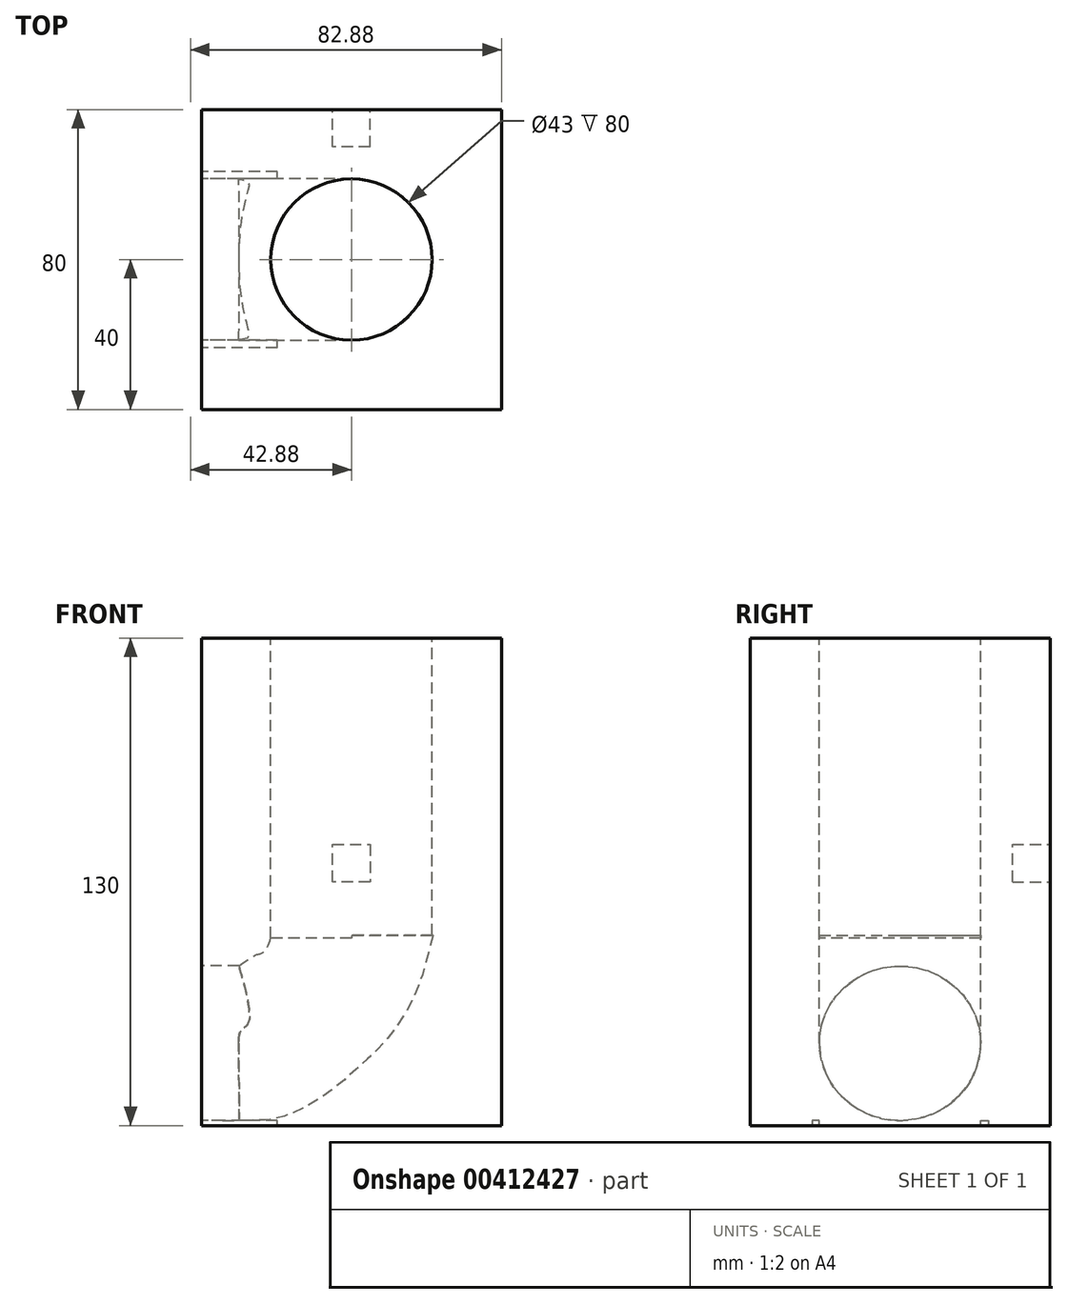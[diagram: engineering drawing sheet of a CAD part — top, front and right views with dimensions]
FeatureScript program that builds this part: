
annotation { "Feature Type Name" : "Feature", "Feature Type Description" : "" }
export const myFeature = defineFeature(function(context is Context, id is Id, definition is map)
    precondition{}
    {
        {
            var Q0;
            Q0=qCreatedBy(makeId("Top.planeOp"),FACE);
            var sketch = newSketch(context, id + "F0", { "sketchPlane" : qUnion([Q0])});
            skLineSegment(sketch, "E0.bottom", {"start": v(40, -40) * mm, "end": v(-40, -40) * mm});
            skLineSegment(sketch, "E0.top", {"start": v(40, 40) * mm, "end": v(-40, 40) * mm});
            skLineSegment(sketch, "E0.left", {"start": v(40, -40) * mm, "end": v(40, 40) * mm});
            skLineSegment(sketch, "E0.right", {"start": v(-40, -40) * mm, "end": v(-40, 40) * mm});
            skPoint(sketch, "E0.middle", {"position": v(0, 0) * mm});
            skSolve(sketch);
        }
        {
            var Q0;
            Q0=makeQuery(id+"F0.imprint","IMPRINT",FACE,{"disambiguationData":[TD([[makeQuery(id+"F0.imprint","IMPRINT",EDGE,{"derivedFrom":sQuery(id+"F0.wireOp",EDGE,"E0.bottom")}),-1.0]])]});
            extrude(context, id + "F1", {"entities" : qUnion([Q0]), "depth" : 130 * mm});
        }
        {
            var Q0;
            Q0=makeQuery(id+"F1.opExtrude","CAP_FACE",FACE,{"disambiguationData":[OSD([sQuery(id+"F0.wireOp",EDGE,"E0.bottom"),sQuery(id+"F0.wireOp",EDGE,"E0.top"),sQuery(id+"F0.wireOp",EDGE,"E0.left"),sQuery(id+"F0.wireOp",EDGE,"E0.right")])],"isStart":false});
            var sketch = newSketch(context, id + "F2", { "sketchPlane" : qUnion([Q0])});
            skCircle(sketch, "E1", {"center": v(0, 0) * mm, "radius": 21.5 * mm});
            skSolve(sketch);
        }
        {
            var Q0;
            Q0=makeQuery(id+"F2.imprint","IMPRINT",FACE,{"disambiguationData":[TD([[makeQuery(id+"F2.imprint","IMPRINT",EDGE,{"derivedFrom":sQuery(id+"F2.wireOp",EDGE,"E1")}),1.0]])]});
            extrude(context, id + "F3", {"entities" : qUnion([Q0]), "operationType" : NewBodyOperationType.REMOVE, "oppositeDirection" : true, "depth" : 80 * mm});
        }
        {
            var Q0;
            Q0=makeQuery(id+"F1.opExtrude","SWEPT_FACE",FACE,{"disambiguationData":[OSD([sQuery(id+"F0.wireOp",EDGE,"E0.top")])]});
            cPlane(context, id + "F4", {"entities" : qUnion([Q0]), "cplaneType" : CPlaneType.OFFSET, "offset" : 40 * mm, "oppositeDirection" : true, "width" : 150 * mm, "height" : 150 * mm});
        }
        {
            var Q0;
            Q0=qCreatedBy(id+"F4.planeOp",FACE);
            var sketch = newSketch(context, id + "F5", { "sketchPlane" : qUnion([Q0])});
            skPoint(sketch, "E2.0.internal.orphan", {"position": v(0, 50.77) * mm});
            skLineSegment(sketch, "E3", {"start": v(40.5, 22.17) * mm, "end": v(30.1, 22.17) * mm});
            skFitSpline(sketch, "E4", {"points": [v(0, 50.77) * mm, v(4.24, 40.15) * mm, v(14.18, 29.43) * mm, v(24.13, 23) * mm, v(30.1, 22.17) * mm], "startDerivative": vector(12.32, -41.84) * mm, "endDerivative": vector(30.55, -0.59) * mm});
            skLineSegment(sketch, "E5", {"start": v(40.5, 22.17) * mm, "end": v(52.8, 22.17) * mm});
            skSolve(sketch);
        }
        {
            var Q0;
            Q0=makeQuery(id+"F3.boolean.opBoolean","COPY",FACE,{"derivedFrom":makeQuery(id+"F3.opExtrude","CAP_FACE",FACE,{"disambiguationData":[OSD([sQuery(id+"F2.wireOp",EDGE,"E1")])],"isStart":false})});
            var Q1;
            Q1=sQuery(id+"F5.wireOp",EDGE,"E4");
            var Q2;
            Q2=sQuery(id+"F5.wireOp",EDGE,"E3");
            var Q3;
            Q3=sQuery(id+"F5.wireOp",EDGE,"E5");
            sweep(context, id + "F6", {"operationType" : NewBodyOperationType.REMOVE, "profiles" : qUnion([Q0]), "path" : qUnion([Q1, Q2, Q3])});
        }
        {
            var Q0;
            Q0=makeQuery(id+"F1.opExtrude","SWEPT_FACE",FACE,{"disambiguationData":[OSD([sQuery(id+"F0.wireOp",EDGE,"E0.right")])]});
            var sketch = newSketch(context, id + "F7", { "sketchPlane" : qUnion([Q0])});
            skLineSegment(sketch, "E6", {"start": v(0, 0) * mm, "end": v(0, 1.33) * mm});
            skLineSegment(sketch, "E7", {"start": v(21.5, 0) * mm, "end": v(21.5, 1.34) * mm});
            skLineSegment(sketch, "E8", {"start": v(21.5, 1.33) * mm, "end": v(23.5, 1.33) * mm});
            skLineSegment(sketch, "E9", {"start": v(23.5, 1.34) * mm, "end": v(23.5, 0) * mm});
            skLineSegment(sketch, "E10", {"start": v(23.5, 0) * mm, "end": v(21.5, 0) * mm});
            skLineSegment(sketch, "E11", {"start": v(-21.5, 0) * mm, "end": v(-21.5, 1.33) * mm});
            skLineSegment(sketch, "E12", {"start": v(-21.5, 1.33) * mm, "end": v(-23.5, 1.33) * mm});
            skLineSegment(sketch, "E13", {"start": v(-23.5, 0) * mm, "end": v(-21.5, 0) * mm});
            skLineSegment(sketch, "E14", {"start": v(-23.5, 1.33) * mm, "end": v(-23.5, 0) * mm});
            skSolve(sketch);
        }
        {
            var Q0;
            Q0=makeQuery(id+"F7.imprint","IMPRINT",FACE,{"disambiguationData":[TD([[makeQuery(id+"F7.imprint","IMPRINT",EDGE,{"derivedFrom":sQuery(id+"F7.wireOp",EDGE,"E11")}),1.0]])]});
            var Q1;
            Q1=makeQuery(id+"F7.imprint","IMPRINT",FACE,{"disambiguationData":[TD([[makeQuery(id+"F7.imprint","IMPRINT",EDGE,{"derivedFrom":sQuery(id+"F7.wireOp",EDGE,"E7")}),-1.0]])]});
            extrude(context, id + "F8", {"entities" : qUnion([Q0, Q1]), "operationType" : NewBodyOperationType.REMOVE, "oppositeDirection" : true, "depth" : 20.2 * mm});
        }
        {
            var Q0;
            Q0=makeQuery(id+"F1.opExtrude","SWEPT_FACE",FACE,{"disambiguationData":[OSD([sQuery(id+"F0.wireOp",EDGE,"E0.top")])]});
            var sketch = newSketch(context, id + "F9", { "sketchPlane" : qUnion([Q0])});
            skLineSegment(sketch, "E15", {"start": v(0, 65) * mm, "end": v(5, 65) * mm});
            skLineSegment(sketch, "E16", {"start": v(5, 65) * mm, "end": v(5, 75) * mm});
            skLineSegment(sketch, "E17", {"start": v(5, 75) * mm, "end": v(-5, 75) * mm});
            skLineSegment(sketch, "E18", {"start": v(-5, 75) * mm, "end": v(-5, 65) * mm});
            skLineSegment(sketch, "E19", {"start": v(-5, 65) * mm, "end": v(0, 65) * mm});
            skPoint(sketch, "E20.start.orphan", {"position": v(0, 0) * mm});
            skSolve(sketch);
        }
        {
            var Q0;
            Q0=makeQuery(id+"F9.imprint","IMPRINT",FACE,{"disambiguationData":[TD([[makeQuery(id+"F9.imprint","IMPRINT",EDGE,{"derivedFrom":sQuery(id+"F9.wireOp",EDGE,"E15")}),1.0]])]});
            extrude(context, id + "F10", {"entities" : qUnion([Q0]), "operationType" : NewBodyOperationType.REMOVE, "oppositeDirection" : true, "depth" : 10 * mm});
        }
    });
